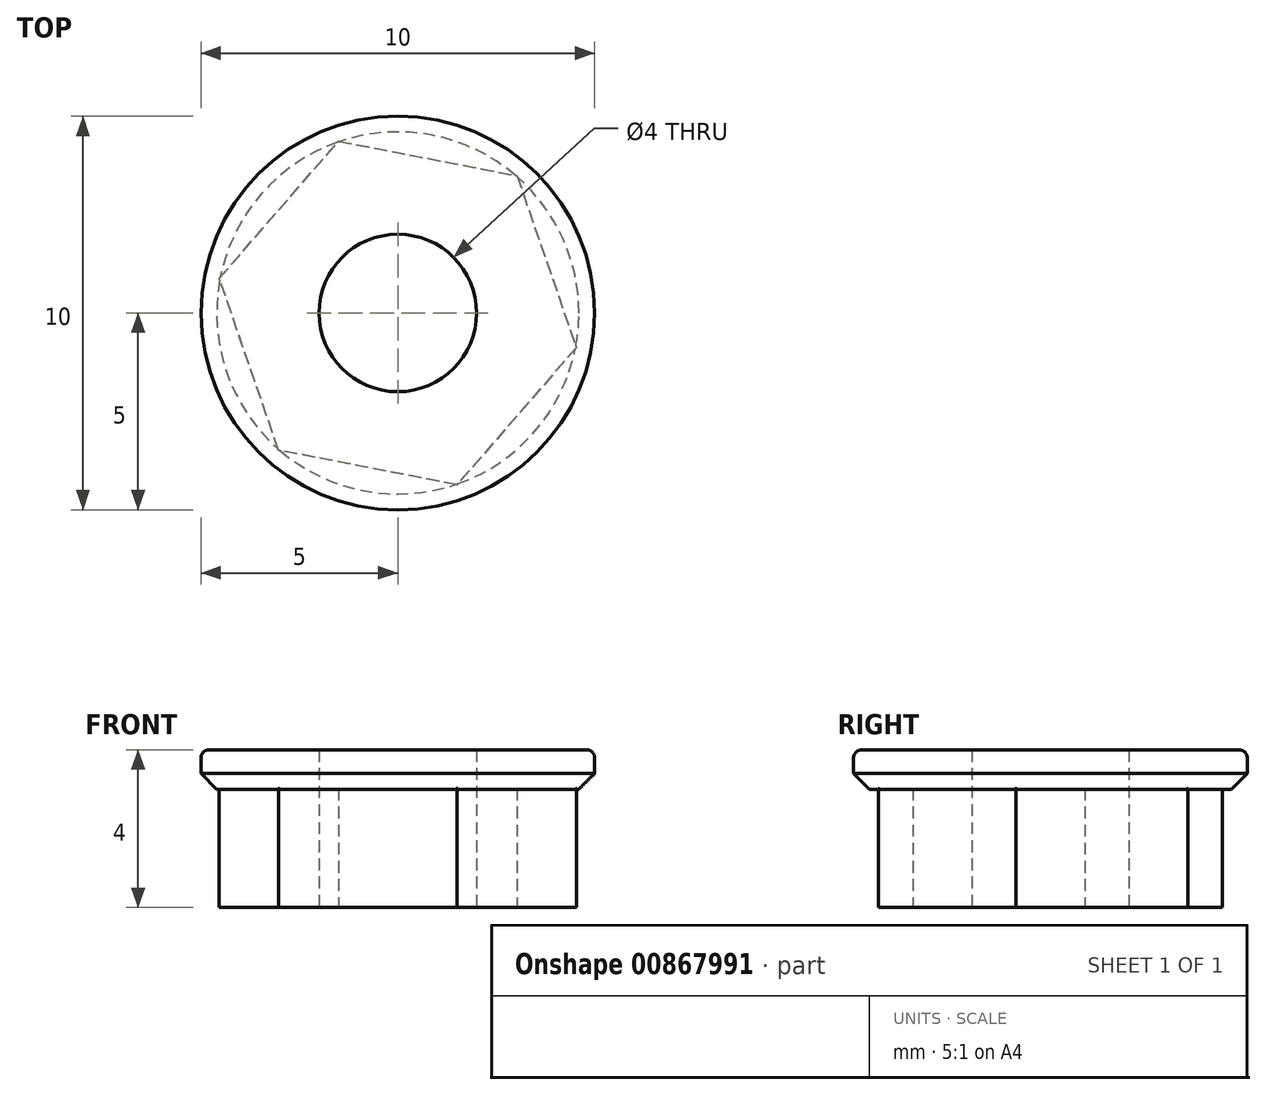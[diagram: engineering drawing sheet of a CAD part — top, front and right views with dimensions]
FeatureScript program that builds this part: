
annotation { "Feature Type Name" : "Feature", "Feature Type Description" : "" }
export const myFeature = defineFeature(function(context is Context, id is Id, definition is map)
    precondition{}
    {
        {
            var Q0;
            Q0=qCreatedBy(makeId("Top.planeOp"),FACE);
            var sketch = newSketch(context, id + "F0", { "sketchPlane" : qUnion([Q0])});
            skCircle(sketch, "E0", {"center": v(0, 0) * mm, "radius": 2 * mm});
            skCircle(sketch, "E1.cCircle", {"center": v(0, 0) * mm, "radius": 4 * mm, "construction": true});
            skLineSegment(sketch, "E1.0", {"start": v(4.53, -0.88) * mm, "end": v(1.5, -4.37) * mm});
            skLineSegment(sketch, "E1.1", {"start": v(1.5, -4.37) * mm, "end": v(-3.03, -3.49) * mm});
            skLineSegment(sketch, "E1.2", {"start": v(-3.03, -3.49) * mm, "end": v(-4.53, 0.88) * mm});
            skLineSegment(sketch, "E1.3", {"start": v(-4.53, 0.88) * mm, "end": v(-1.5, 4.37) * mm});
            skLineSegment(sketch, "E1.4", {"start": v(-1.5, 4.37) * mm, "end": v(3.03, 3.49) * mm});
            skLineSegment(sketch, "E1.5", {"start": v(3.03, 3.49) * mm, "end": v(4.53, -0.88) * mm});
            skPoint(sketch, "E1.0.midPoint", {"position": v(3.02, -2.62) * mm});
            skSolve(sketch);
        }
        {
            var Q0;
            Q0=makeQuery(id+"F0.imprint","IMPRINT",FACE,{"disambiguationData":[TD([[makeQuery(id+"F0.imprint","IMPRINT",EDGE,{"derivedFrom":sQuery(id+"F0.wireOp",EDGE,"E0")}),-1.0]])]});
            extrude(context, id + "F1", {"entities" : qUnion([Q0]), "depth" : 3 * mm, "offsetDistance" : 25 * mm});
        }
        {
            var Q0;
            Q0=makeQuery(id+"F1.opExtrude","CAP_FACE",FACE,{"disambiguationData":[OSD([sQuery(id+"F0.wireOp",EDGE,"E0"),sQuery(id+"F0.wireOp",EDGE,"E1.0"),sQuery(id+"F0.wireOp",EDGE,"E1.1"),sQuery(id+"F0.wireOp",EDGE,"E1.2"),sQuery(id+"F0.wireOp",EDGE,"E1.3"),sQuery(id+"F0.wireOp",EDGE,"E1.4"),sQuery(id+"F0.wireOp",EDGE,"E1.5")])],"isStart":false});
            var sketch = newSketch(context, id + "F2", { "sketchPlane" : qUnion([Q0])});
            skCircle(sketch, "E2", {"center": v(0, 0) * mm, "radius": 2 * mm});
            skCircle(sketch, "E3", {"center": v(0, 0) * mm, "radius": 5 * mm});
            skSolve(sketch);
        }
        {
            var Q0;
            Q0 = qSketchRegion(id + "F2", true);
            extrude(context, id + "F3", {"entities" : qUnion([Q0]), "operationType" : NewBodyOperationType.ADD, "depth" : 1 * mm, "offsetDistance" : 25 * mm});
        }
        {
            var Q0;
            Q0=makeQuery(id+"F3.opExtrude","CAP_EDGE",EDGE,{"disambiguationData":[OSD([sQuery(id+"F2.wireOp",EDGE,"E3")])],"isStart":true});
            chamfer(context, id + "F4", {"entities" : qUnion([Q0]), "width" : 0.4 * mm, "tangentPropagation" : true});
        }
        {
            var Q0;
            Q0=makeQuery(id+"F3.opExtrude","CAP_EDGE",EDGE,{"disambiguationData":[OSD([sQuery(id+"F2.wireOp",EDGE,"E3")])],"isStart":false});
            fillet(context, id + "F5", {"entities" : qUnion([Q0]), "radius" : 0.2 * mm, "tangentPropagation" : true, "allowEdgeOverflow" : false});
        }
    });
